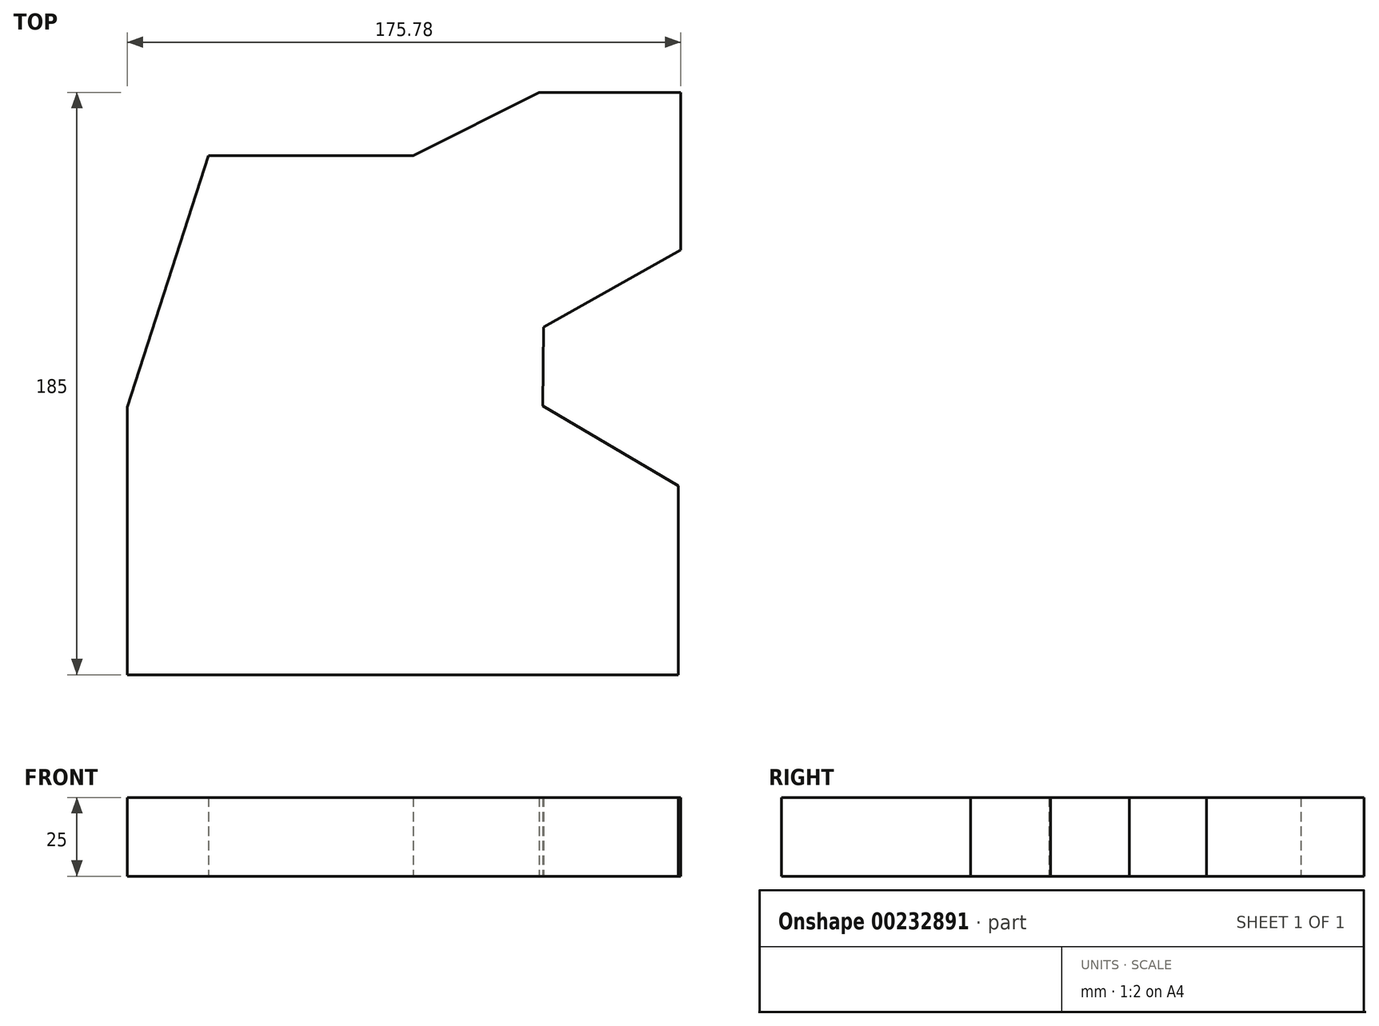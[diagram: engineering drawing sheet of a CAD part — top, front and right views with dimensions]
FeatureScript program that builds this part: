
annotation { "Feature Type Name" : "Feature", "Feature Type Description" : "" }
export const myFeature = defineFeature(function(context is Context, id is Id, definition is map)
    precondition{}
    {
        {
            var Q0;
            Q0=qCreatedBy(makeId("Top.planeOp"),FACE);
            var sketch = newSketch(context, id + "F0", { "sketchPlane" : qUnion([Q0])});
            skLineSegment(sketch, "E0", {"start": v(-114.71, -108.63) * mm, "end": v(-114.71, -23.63) * mm});
            skLineSegment(sketch, "E1", {"start": v(-114.71, -23.63) * mm, "end": v(-114.71, -108.63) * mm});
            skLineSegment(sketch, "E2", {"start": v(-114.71, -108.63) * mm, "end": v(60.29, -108.63) * mm});
            skLineSegment(sketch, "E3", {"start": v(60.29, -108.63) * mm, "end": v(60.29, -48.63) * mm});
            skLineSegment(sketch, "E4", {"start": v(-114.71, -23.63) * mm, "end": v(-88.93, 56.37) * mm});
            skLineSegment(sketch, "E5", {"start": v(-88.93, 56.37) * mm, "end": v(-23.93, 56.37) * mm});
            skLineSegment(sketch, "E6", {"start": v(-23.93, 56.37) * mm, "end": v(16.07, 76.37) * mm});
            skLineSegment(sketch, "E7", {"start": v(16.07, 76.37) * mm, "end": v(61.07, 76.37) * mm});
            skLineSegment(sketch, "E8", {"start": v(61.07, 76.37) * mm, "end": v(61.07, 26.37) * mm});
            skLineSegment(sketch, "E9", {"start": v(61.07, 26.37) * mm, "end": v(17.5, 1.81) * mm});
            skLineSegment(sketch, "E10", {"start": v(60.29, -48.63) * mm, "end": v(17.25, -23.19) * mm});
            skLineSegment(sketch, "E11", {"start": v(17.25, -23.19) * mm, "end": v(17.5, 1.81) * mm});
            skSolve(sketch);
        }
        {
            var Q0;
            Q0 = qSketchRegion(id + "F0", true);
            extrude(context, id + "F1", {"entities" : qUnion([Q0]), "depth" : 25 * mm});
        }
    });
